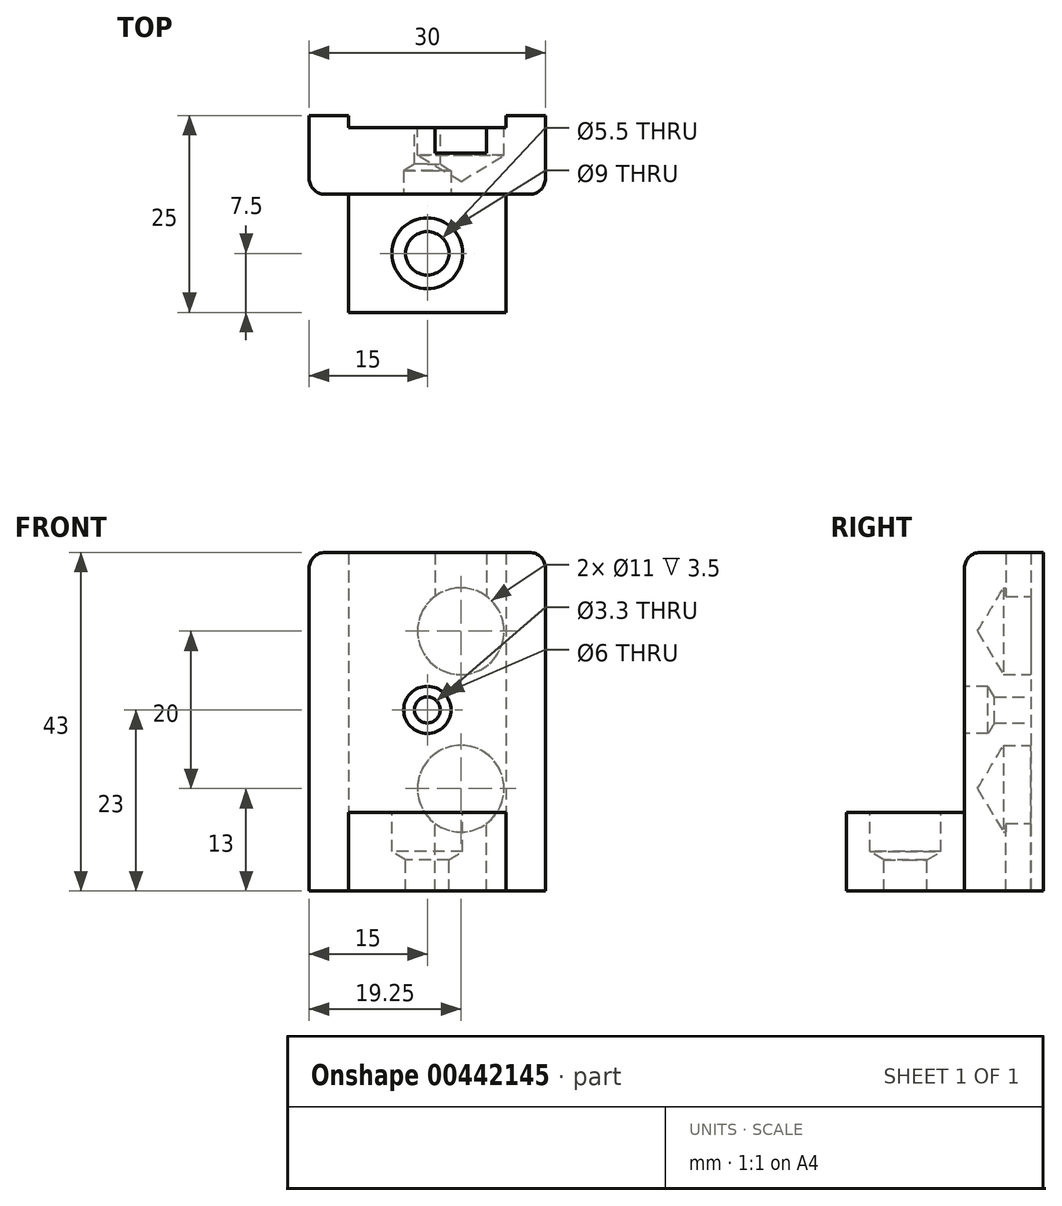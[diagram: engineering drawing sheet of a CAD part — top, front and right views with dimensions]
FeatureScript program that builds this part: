
annotation { "Feature Type Name" : "Feature", "Feature Type Description" : "" }
export const myFeature = defineFeature(function(context is Context, id is Id, definition is map)
    precondition{}
    {
        {
            var Q0;
            Q0=qCreatedBy(makeId("Front.planeOp"),FACE);
            var sketch = newSketch(context, id + "F0", { "sketchPlane" : qUnion([Q0])});
            skLineSegment(sketch, "E0.bottom", {"start": v(15, -21.5) * mm, "end": v(-15, -21.5) * mm});
            skLineSegment(sketch, "E0.top", {"start": v(15, 21.5) * mm, "end": v(-15, 21.5) * mm});
            skLineSegment(sketch, "E0.left", {"start": v(15, -21.5) * mm, "end": v(15, 21.5) * mm});
            skLineSegment(sketch, "E0.right", {"start": v(-15, -21.5) * mm, "end": v(-15, 21.5) * mm});
            skPoint(sketch, "E0.middle", {"position": v(0, 0) * mm});
            skSolve(sketch);
        }
        {
            var Q0;
            Q0=makeQuery(id+"F0.imprint","IMPRINT",FACE,{"disambiguationData":[TD([[makeQuery(id+"F0.imprint","IMPRINT",EDGE,{"derivedFrom":sQuery(id+"F0.wireOp",EDGE,"E0.bottom")}),-1.0]])]});
            extrude(context, id + "F1", {"entities" : qUnion([Q0]), "depth" : 10 * mm, "offsetDistance" : 25 * mm});
        }
        {
            var Q0;
            Q0=makeQuery(id+"F1.opExtrude","CAP_FACE",FACE,{"disambiguationData":[OSD([sQuery(id+"F0.wireOp",EDGE,"E0.bottom"),sQuery(id+"F0.wireOp",EDGE,"E0.top"),sQuery(id+"F0.wireOp",EDGE,"E0.left"),sQuery(id+"F0.wireOp",EDGE,"E0.right")])],"isStart":false});
            var sketch = newSketch(context, id + "F2", { "sketchPlane" : qUnion([Q0])});
            skLineSegment(sketch, "E1.bottom", {"start": v(-10, -21.5) * mm, "end": v(10, -21.5) * mm});
            skLineSegment(sketch, "E1.top", {"start": v(-10, -11.5) * mm, "end": v(10, -11.5) * mm});
            skLineSegment(sketch, "E1.left", {"start": v(-10, -21.5) * mm, "end": v(-10, -11.5) * mm});
            skLineSegment(sketch, "E1.right", {"start": v(10, -21.5) * mm, "end": v(10, -11.5) * mm});
            skSolve(sketch);
        }
        {
            var Q0;
            Q0=makeQuery(id+"F2.imprint","IMPRINT",FACE,{"disambiguationData":[TD([[makeQuery(id+"F2.imprint","IMPRINT",EDGE,{"derivedFrom":sQuery(id+"F2.wireOp",EDGE,"E1.bottom")}),-1.0]])]});
            extrude(context, id + "F3", {"entities" : qUnion([Q0]), "operationType" : NewBodyOperationType.ADD, "depth" : 15 * mm, "offsetDistance" : 25 * mm});
        }
        {
            var Q0;
            Q0=makeQuery(id+"F3.opExtrude","SWEPT_FACE",FACE,{"disambiguationData":[OSD([sQuery(id+"F2.wireOp",EDGE,"E1.top")])]});
            var sketch = newSketch(context, id + "F4", { "sketchPlane" : qUnion([Q0])});
            skPoint(sketch, "E2", {"position": v(0, -17.5) * mm});
            skPoint(sketch, "E2.positionSnap0", {"position": v(10, -17.5) * mm});
            skSolve(sketch);
        }
        {
            var Q0;
            Q0=sQuery(id+"F4.wireOp",VERTEX,"E2");
            var Q1;
            Q1=makeQuery(id+"F1.opExtrude","SWEPT_BODY",BODY,{"disambiguationData":[OSD([sQuery(id+"F0.wireOp",EDGE,"E0.bottom"),sQuery(id+"F0.wireOp",EDGE,"E0.top"),sQuery(id+"F0.wireOp",EDGE,"E0.left"),sQuery(id+"F0.wireOp",EDGE,"E0.right")])]});
            hole(context, id + "F5", {"style" : HoleStyle.SIMPLE, "endStyle" : HoleEndStyle.THROUGH, "standardTappedOrClearance" : lookupTablePath({ "standard" : "ISO", "fit" : "Normal", "size" : "M5", "type" : "Clearance" }), "standardBlindInLast" : lookupTablePath({ "fit" : "Standard", "standard" : "ISO", "size" : "M5", "type" : "Clearance" }), "holeDiameter" : 5.5 * mm, "isTappedThrough" : true, "tappedDepth" : 12 * mm, "tapClearance" : 3, "startFromSketch" : true, "locations" : qUnion([Q0]), "scope" : qUnion([Q1])});
        }
        {
            var Q0;
            Q0=makeQuery(id+"F3.opExtrude","SWEPT_FACE",FACE,{"disambiguationData":[OSD([sQuery(id+"F2.wireOp",EDGE,"E1.top")])]});
            var sketch = newSketch(context, id + "F6", { "sketchPlane" : qUnion([Q0])});
            skPoint(sketch, "E3", {"position": v(0, -17.5) * mm});
            skSolve(sketch);
        }
        {
            var Q0;
            Q0=sQuery(id+"F6.wireOp",VERTEX,"E3");
            var Q1;
            Q1=makeQuery(id+"F1.opExtrude","SWEPT_BODY",BODY,{"disambiguationData":[OSD([sQuery(id+"F0.wireOp",EDGE,"E0.bottom"),sQuery(id+"F0.wireOp",EDGE,"E0.top"),sQuery(id+"F0.wireOp",EDGE,"E0.left"),sQuery(id+"F0.wireOp",EDGE,"E0.right")])]});
            hole(context, id + "F7", {"style" : HoleStyle.SIMPLE, "endStyle" : HoleEndStyle.BLIND, "holeDiameter" : 9 * mm, "holeDepth" : 5 * mm, "isTappedThrough" : true, "tappedDepth" : 12 * mm, "tapClearance" : 3, "startFromSketch" : true, "locations" : qUnion([Q0]), "scope" : qUnion([Q1])});
        }
        {
            var Q0;
            Q0=makeQuery(id+"F1.opExtrude","CAP_FACE",FACE,{"disambiguationData":[OSD([sQuery(id+"F0.wireOp",EDGE,"E0.bottom"),sQuery(id+"F0.wireOp",EDGE,"E0.top"),sQuery(id+"F0.wireOp",EDGE,"E0.left"),sQuery(id+"F0.wireOp",EDGE,"E0.right")])],"isStart":true});
            var sketch = newSketch(context, id + "F8", { "sketchPlane" : qUnion([Q0])});
            skLineSegment(sketch, "E4.bottom", {"start": v(-10, 21.5) * mm, "end": v(10, 21.5) * mm});
            skLineSegment(sketch, "E4.top", {"start": v(-10, -21.5) * mm, "end": v(10, -21.5) * mm});
            skLineSegment(sketch, "E4.left", {"start": v(-10, 21.5) * mm, "end": v(-10, -21.5) * mm});
            skLineSegment(sketch, "E4.right", {"start": v(10, 21.5) * mm, "end": v(10, -21.5) * mm});
            skPoint(sketch, "E5", {"position": v(0, 0) * mm});
            skSolve(sketch);
        }
        {
            var Q0;
            Q0=makeQuery(id+"F8.imprint","IMPRINT",FACE,{"disambiguationData":[TD([[makeQuery(id+"F8.imprint","IMPRINT",EDGE,{"derivedFrom":sQuery(id+"F8.wireOp",EDGE,"E4.bottom")}),-1.0]])]});
            extrude(context, id + "F9", {"entities" : qUnion([Q0]), "operationType" : NewBodyOperationType.REMOVE, "oppositeDirection" : true, "depth" : 1.55 * mm, "offsetDistance" : 25 * mm});
        }
        {
            var Q0;
            Q0=makeQuery(id+"F9.boolean.opBoolean","COPY",FACE,{"derivedFrom":makeQuery(id+"F9.opExtrude","CAP_FACE",FACE,{"disambiguationData":[OSD([sQuery(id+"F8.wireOp",EDGE,"E4.bottom"),sQuery(id+"F8.wireOp",EDGE,"E4.top"),sQuery(id+"F8.wireOp",EDGE,"E4.left"),sQuery(id+"F8.wireOp",EDGE,"E4.right")])],"isStart":false})});
            var sketch = newSketch(context, id + "F10", { "sketchPlane" : qUnion([Q0])});
            skPoint(sketch, "E6", {"position": v(0, 1.5) * mm});
            skSolve(sketch);
        }
        {
            var Q0;
            Q0=sQuery(id+"F10.wireOp",VERTEX,"E6");
            var Q1;
            Q1=makeQuery(id+"F1.opExtrude","SWEPT_BODY",BODY,{"disambiguationData":[OSD([sQuery(id+"F0.wireOp",EDGE,"E0.bottom"),sQuery(id+"F0.wireOp",EDGE,"E0.top"),sQuery(id+"F0.wireOp",EDGE,"E0.left"),sQuery(id+"F0.wireOp",EDGE,"E0.right")])]});
            hole(context, id + "F11", {"style" : HoleStyle.SIMPLE, "endStyle" : HoleEndStyle.THROUGH, "standardTappedOrClearance" : lookupTablePath({ "standard" : "ISO", "fit" : "Normal", "size" : "M3", "type" : "Clearance" }), "standardBlindInLast" : lookupTablePath({ "fit" : "Standard", "standard" : "ISO", "size" : "M3", "type" : "Clearance" }), "holeDiameter" : 3.3 * mm, "isTappedThrough" : true, "tappedDepth" : 12 * mm, "tapClearance" : 3, "startFromSketch" : true, "locations" : qUnion([Q0]), "scope" : qUnion([Q1])});
        }
        {
            var Q0;
            Q0=makeQuery(id+"F1.opExtrude","CAP_FACE",FACE,{"disambiguationData":[OSD([sQuery(id+"F0.wireOp",EDGE,"E0.bottom"),sQuery(id+"F0.wireOp",EDGE,"E0.top"),sQuery(id+"F0.wireOp",EDGE,"E0.left"),sQuery(id+"F0.wireOp",EDGE,"E0.right")])],"isStart":false});
            var sketch = newSketch(context, id + "F12", { "sketchPlane" : qUnion([Q0])});
            skPoint(sketch, "E7", {"position": v(0, 1.5) * mm});
            skSolve(sketch);
        }
        {
            var Q0;
            Q0=sQuery(id+"F12.wireOp",VERTEX,"E7");
            var Q1;
            Q1=makeQuery(id+"F1.opExtrude","SWEPT_BODY",BODY,{"disambiguationData":[OSD([sQuery(id+"F0.wireOp",EDGE,"E0.bottom"),sQuery(id+"F0.wireOp",EDGE,"E0.top"),sQuery(id+"F0.wireOp",EDGE,"E0.left"),sQuery(id+"F0.wireOp",EDGE,"E0.right")])]});
            hole(context, id + "F13", {"style" : HoleStyle.SIMPLE, "endStyle" : HoleEndStyle.BLIND, "holeDiameter" : 6 * mm, "holeDepth" : 3 * mm, "isTappedThrough" : true, "tappedDepth" : 12 * mm, "tapClearance" : 3, "startFromSketch" : true, "locations" : qUnion([Q0]), "scope" : qUnion([Q1])});
        }
        {
            var Q0;
            Q0=makeQuery(id+"F9.boolean.opBoolean","COPY",FACE,{"derivedFrom":makeQuery(id+"F9.opExtrude","CAP_FACE",FACE,{"disambiguationData":[OSD([sQuery(id+"F8.wireOp",EDGE,"E4.bottom"),sQuery(id+"F8.wireOp",EDGE,"E4.top"),sQuery(id+"F8.wireOp",EDGE,"E4.left"),sQuery(id+"F8.wireOp",EDGE,"E4.right")])],"isStart":false})});
            var sketch = newSketch(context, id + "F14", { "sketchPlane" : qUnion([Q0])});
            skLineSegment(sketch, "E8.bottom", {"start": v(-7.5, 21.5) * mm, "end": v(-1, 21.5) * mm});
            skLineSegment(sketch, "E8.top", {"start": v(-7.5, 11.5) * mm, "end": v(-1, 11.5) * mm});
            skLineSegment(sketch, "E8.left", {"start": v(-7.5, 21.5) * mm, "end": v(-7.5, 11.5) * mm});
            skLineSegment(sketch, "E8.right", {"start": v(-1, 21.5) * mm, "end": v(-1, 11.5) * mm});
            skLineSegment(sketch, "E9.MirrorCS", {"start": v(-7.5, -11.5) * mm, "end": v(-1, -11.5) * mm});
            skLineSegment(sketch, "E10.MirrorCS", {"start": v(-7.5, -21.5) * mm, "end": v(-7.5, -11.5) * mm});
            skLineSegment(sketch, "E11.MirrorCS", {"start": v(-7.5, -21.5) * mm, "end": v(-1, -21.5) * mm});
            skLineSegment(sketch, "E12.MirrorCS", {"start": v(-1, -21.5) * mm, "end": v(-1, -11.5) * mm});
            skSolve(sketch);
        }
        {
            var Q0;
            Q0=makeQuery(id+"F14.imprint","IMPRINT",FACE,{"disambiguationData":[TD([[makeQuery(id+"F14.imprint","IMPRINT",EDGE,{"derivedFrom":sQuery(id+"F14.wireOp",EDGE,"E8.bottom")}),-1.0]])]});
            var Q1;
            Q1=makeQuery(id+"F14.imprint","IMPRINT",FACE,{"disambiguationData":[TD([[makeQuery(id+"F14.imprint","IMPRINT",EDGE,{"derivedFrom":sQuery(id+"F14.wireOp",EDGE,"E9.MirrorCS")}),-1.0]])]});
            extrude(context, id + "F15", {"entities" : qUnion([Q0, Q1]), "operationType" : NewBodyOperationType.REMOVE, "oppositeDirection" : true, "depth" : 3.2 * mm, "offsetDistance" : 25 * mm});
        }
        {
            var Q0;
            Q0=makeQuery(id+"F9.boolean.opBoolean","COPY",FACE,{"derivedFrom":makeQuery(id+"F9.opExtrude","CAP_FACE",FACE,{"disambiguationData":[OSD([sQuery(id+"F8.wireOp",EDGE,"E4.bottom"),sQuery(id+"F8.wireOp",EDGE,"E4.top"),sQuery(id+"F8.wireOp",EDGE,"E4.left"),sQuery(id+"F8.wireOp",EDGE,"E4.right")])],"isStart":false})});
            var sketch = newSketch(context, id + "F16", { "sketchPlane" : qUnion([Q0])});
            skPoint(sketch, "E13", {"position": v(-4.25, 11.5) * mm});
            skPoint(sketch, "E13.positionSnap0", {"position": v(-4.25, 11.5) * mm});
            skPoint(sketch, "E14", {"position": v(-4.25, -8.5) * mm});
            skPoint(sketch, "E14.positionSnap0", {"position": v(-4.25, -11.5) * mm});
            skSolve(sketch);
        }
        {
            var Q0;
            Q0=sQuery(id+"F16.wireOp",VERTEX,"E14");
            var Q1;
            Q1=sQuery(id+"F16.wireOp",VERTEX,"E13");
            var Q2;
            Q2=makeQuery(id+"F1.opExtrude","SWEPT_BODY",BODY,{"disambiguationData":[OSD([sQuery(id+"F0.wireOp",EDGE,"E0.bottom"),sQuery(id+"F0.wireOp",EDGE,"E0.top"),sQuery(id+"F0.wireOp",EDGE,"E0.left"),sQuery(id+"F0.wireOp",EDGE,"E0.right")])]});
            hole(context, id + "F17", {"style" : HoleStyle.SIMPLE, "endStyle" : HoleEndStyle.BLIND, "holeDiameter" : 11 * mm, "holeDepth" : 3.5 * mm, "isTappedThrough" : true, "tappedDepth" : 12 * mm, "tapClearance" : 3, "startFromSketch" : true, "locations" : qUnion([Q0, Q1]), "scope" : qUnion([Q2])});
        }
        {
            var Q0;
            Q0=makeQuery(id+"F1.opExtrude","SWEPT_EDGE",EDGE,{"disambiguationData":[OSD([sQuery(id+"F0.wireOp",EDGE,"E0.top"),sQuery(id+"F0.wireOp",EDGE,"E0.right")])]});
            var Q1;
            Q1=makeQuery(id+"F1.opExtrude","CAP_EDGE",EDGE,{"disambiguationData":[OSD([sQuery(id+"F0.wireOp",EDGE,"E0.top")])],"isStart":false});
            var Q2;
            Q2=makeQuery(id+"F1.opExtrude","CAP_EDGE",EDGE,{"disambiguationData":[OSD([sQuery(id+"F0.wireOp",EDGE,"E0.right")])],"isStart":false});
            var Q3;
            Q3=makeQuery(id+"F1.opExtrude","SWEPT_EDGE",EDGE,{"disambiguationData":[OSD([sQuery(id+"F0.wireOp",EDGE,"E0.top"),sQuery(id+"F0.wireOp",EDGE,"E0.left")])]});
            var Q4;
            Q4=makeQuery(id+"F1.opExtrude","CAP_EDGE",EDGE,{"disambiguationData":[OSD([sQuery(id+"F0.wireOp",EDGE,"E0.left")])],"isStart":false});
            fillet(context, id + "F18", {"entities" : qUnion([Q0, Q1, Q2, Q3, Q4]), "radius" : 2 * mm, "tangentPropagation" : true, "allowEdgeOverflow" : false});
        }
    });
